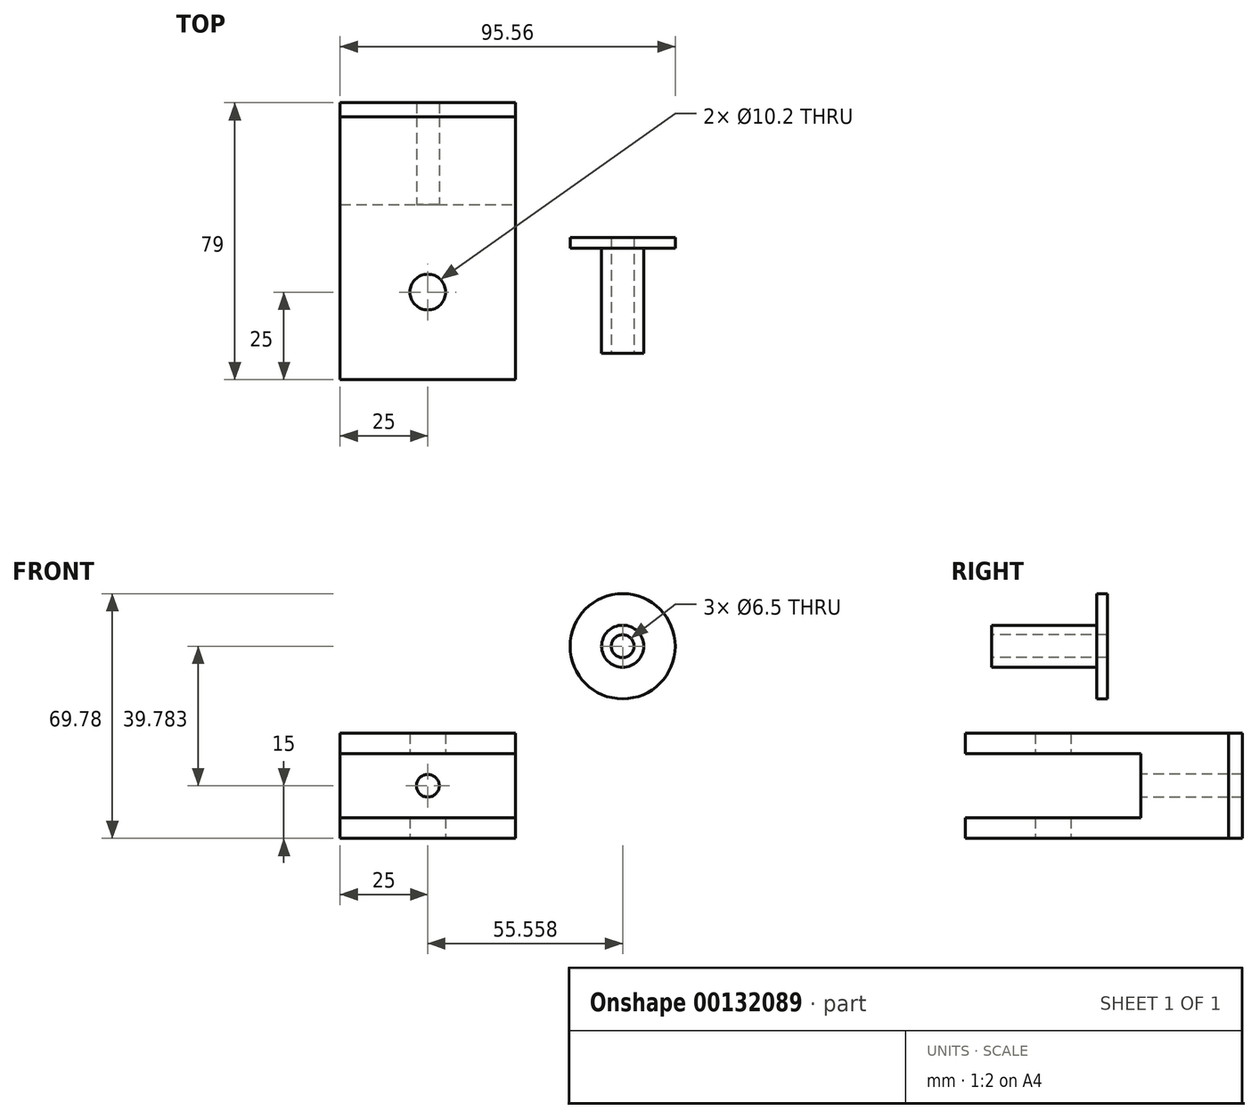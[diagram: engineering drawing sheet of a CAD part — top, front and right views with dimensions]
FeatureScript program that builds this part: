
annotation { "Feature Type Name" : "Feature", "Feature Type Description" : "" }
export const myFeature = defineFeature(function(context is Context, id is Id, definition is map)
    precondition{}
    {
        {
            var Q0;
            Q0=qCreatedBy(makeId("Top.planeOp"),FACE);
            var sketch = newSketch(context, id + "F0", { "sketchPlane" : qUnion([Q0])});
            skLineSegment(sketch, "E0.bottom", {"start": v(-25, 37.5) * mm, "end": v(25, 37.5) * mm});
            skLineSegment(sketch, "E0.top", {"start": v(-25, -37.5) * mm, "end": v(25, -37.5) * mm});
            skLineSegment(sketch, "E0.left", {"start": v(-25, 37.5) * mm, "end": v(-25, -37.5) * mm});
            skLineSegment(sketch, "E0.right", {"start": v(25, 37.5) * mm, "end": v(25, -37.5) * mm});
            skPoint(sketch, "E0.middle", {"position": v(0, 0) * mm});
            skSolve(sketch);
        }
        {
            var Q0;
            Q0=makeQuery(id+"F0.imprint","IMPRINT",FACE,{"disambiguationData":[TD([[makeQuery(id+"F0.imprint","IMPRINT",EDGE,{"derivedFrom":sQuery(id+"F0.wireOp",EDGE,"E0.bottom")}),-1.0]])]});
            extrude(context, id + "F1", {"entities" : qUnion([Q0]), "depth" : 30 * mm});
        }
        {
            var Q0;
            Q0=makeQuery(id+"F1.opExtrude","SWEPT_FACE",FACE,{"disambiguationData":[OSD([sQuery(id+"F0.wireOp",EDGE,"E0.top")])]});
            var sketch = newSketch(context, id + "F2", { "sketchPlane" : qUnion([Q0])});
            skLineSegment(sketch, "E1.0.0", {"start": v(-25, 0) * mm, "end": v(25, 0) * mm});
            skLineSegment(sketch, "E1.0.1", {"start": v(25, 0) * mm, "end": v(25, 30) * mm});
            skLineSegment(sketch, "E1.0.2", {"start": v(25, 30) * mm, "end": v(-25, 30) * mm});
            skLineSegment(sketch, "E1.0.3", {"start": v(-25, 30) * mm, "end": v(-25, 0) * mm});
            skLineSegment(sketch, "E2", {"start": v(-25, 15) * mm, "end": v(25, 15) * mm, "construction": true});
            skLineSegment(sketch, "E3.bottom", {"start": v(-25, 24.15) * mm, "end": v(25, 24.15) * mm});
            skLineSegment(sketch, "E3.top", {"start": v(-25, 5.85) * mm, "end": v(25, 5.85) * mm});
            skLineSegment(sketch, "E3.left", {"start": v(-25, 24.15) * mm, "end": v(-25, 5.85) * mm});
            skLineSegment(sketch, "E3.right", {"start": v(25, 24.15) * mm, "end": v(25, 5.85) * mm});
            skPoint(sketch, "E3.middle", {"position": v(0, 15) * mm});
            skSolve(sketch);
        }
        {
            var Q0;
            Q0=makeQuery(id+"F2.imprint","IMPRINT",FACE,{"disambiguationData":[TD([[makeQuery(id+"F2.imprint","IMPRINT",EDGE,{"derivedFrom":sQuery(id+"F2.wireOp",EDGE,"E3.bottom")}),-1.0]])]});
            extrude(context, id + "F3", {"entities" : qUnion([Q0]), "operationType" : NewBodyOperationType.REMOVE, "oppositeDirection" : true, "depth" : 50 * mm});
        }
        {
            var Q0;
            Q0=sQuery(id+"F2.wireOp",VERTEX,"E3.middle");
            var Q1;
            Q1=makeQuery(id+"F1.opExtrude","SWEPT_BODY",BODY,{"disambiguationData":[OSD([sQuery(id+"F0.wireOp",EDGE,"E0.bottom"),sQuery(id+"F0.wireOp",EDGE,"E0.top"),sQuery(id+"F0.wireOp",EDGE,"E0.left"),sQuery(id+"F0.wireOp",EDGE,"E0.right")])]});
            hole(context, id + "F4", {"style" : HoleStyle.SIMPLE, "endStyle" : HoleEndStyle.THROUGH, "holeDiameter" : 6.5 * mm, "locations" : qUnion([Q0]), "scope" : qUnion([Q1]), "isTappedThrough" : true});
        }
        {
            var Q0;
            Q0=makeQuery(id+"F1.opExtrude","CAP_FACE",FACE,{"disambiguationData":[OSD([sQuery(id+"F0.wireOp",EDGE,"E0.bottom"),sQuery(id+"F0.wireOp",EDGE,"E0.top"),sQuery(id+"F0.wireOp",EDGE,"E0.left"),sQuery(id+"F0.wireOp",EDGE,"E0.right")])],"isStart":true});
            var sketch = newSketch(context, id + "F5", { "sketchPlane" : qUnion([Q0])});
            skLineSegment(sketch, "E4.0.0", {"start": v(-25, -37.5) * mm, "end": v(25, -37.5) * mm});
            skLineSegment(sketch, "E4.0.1", {"start": v(25, -37.5) * mm, "end": v(25, 37.5) * mm});
            skLineSegment(sketch, "E4.0.2", {"start": v(25, 37.5) * mm, "end": v(-25, 37.5) * mm});
            skLineSegment(sketch, "E4.0.3", {"start": v(-25, 37.5) * mm, "end": v(-25, -37.5) * mm});
            skLineSegment(sketch, "E5.0", {"start": v(-25, -12.5) * mm, "end": v(25, -12.5) * mm});
            skPoint(sketch, "E6", {"position": v(0, 12.5) * mm});
            skSolve(sketch);
        }
        {
            var Q0;
            Q0=sQuery(id+"F5.wireOp",VERTEX,"E6");
            var Q1;
            Q1=makeQuery(id+"F1.opExtrude","SWEPT_BODY",BODY,{"disambiguationData":[OSD([sQuery(id+"F0.wireOp",EDGE,"E0.bottom"),sQuery(id+"F0.wireOp",EDGE,"E0.top"),sQuery(id+"F0.wireOp",EDGE,"E0.left"),sQuery(id+"F0.wireOp",EDGE,"E0.right")])]});
            hole(context, id + "F6", {"style" : HoleStyle.SIMPLE, "endStyle" : HoleEndStyle.THROUGH, "holeDiameter" : 10.2 * mm, "locations" : qUnion([Q0]), "scope" : qUnion([Q1]), "isTappedThrough" : true});
        }
        {
            var Q0;
            Q0=qCreatedBy(makeId("Front.planeOp"),FACE);
            var sketch = newSketch(context, id + "F7", { "sketchPlane" : qUnion([Q0])});
            skCircle(sketch, "E7", {"center": v(55.56, 54.78) * mm, "radius": 15 * mm});
            skCircle(sketch, "E8", {"center": v(55.56, 54.78) * mm, "radius": 3.25 * mm});
            skCircle(sketch, "E9", {"center": v(55.56, 54.78) * mm, "radius": 6 * mm});
            skSolve(sketch);
        }
        {
            var Q0;
            Q0=makeQuery(id+"F7.imprint","IMPRINT",FACE,{"disambiguationData":[TD([[makeQuery(id+"F7.imprint","IMPRINT",EDGE,{"derivedFrom":sQuery(id+"F7.wireOp",EDGE,"E7")}),1.0]])]});
            var Q1;
            Q1=makeQuery(id+"F7.imprint","IMPRINT",FACE,{"disambiguationData":[TD([[makeQuery(id+"F7.imprint","IMPRINT",EDGE,{"derivedFrom":sQuery(id+"F7.wireOp",EDGE,"E8")}),-1.0]])]});
            extrude(context, id + "F8", {"entities" : qUnion([Q0, Q1]), "oppositeDirection" : true, "depth" : 3 * mm});
        }
        {
            var Q0;
            Q0=makeQuery(id+"F7.imprint","IMPRINT",FACE,{"disambiguationData":[TD([[makeQuery(id+"F7.imprint","IMPRINT",EDGE,{"derivedFrom":sQuery(id+"F7.wireOp",EDGE,"E8")}),-1.0]])]});
            extrude(context, id + "F9", {"entities" : qUnion([Q0]), "operationType" : NewBodyOperationType.ADD, "depth" : 30 * mm});
        }
        {
            var Q0;
            Q0=makeQuery(id+"F1.opExtrude","SWEPT_FACE",FACE,{"disambiguationData":[OSD([sQuery(id+"F0.wireOp",EDGE,"E0.bottom")])]});
            extrude(context, id + "F10", {"entities" : qUnion([Q0]), "depth" : 4 * mm});
        }
    });
